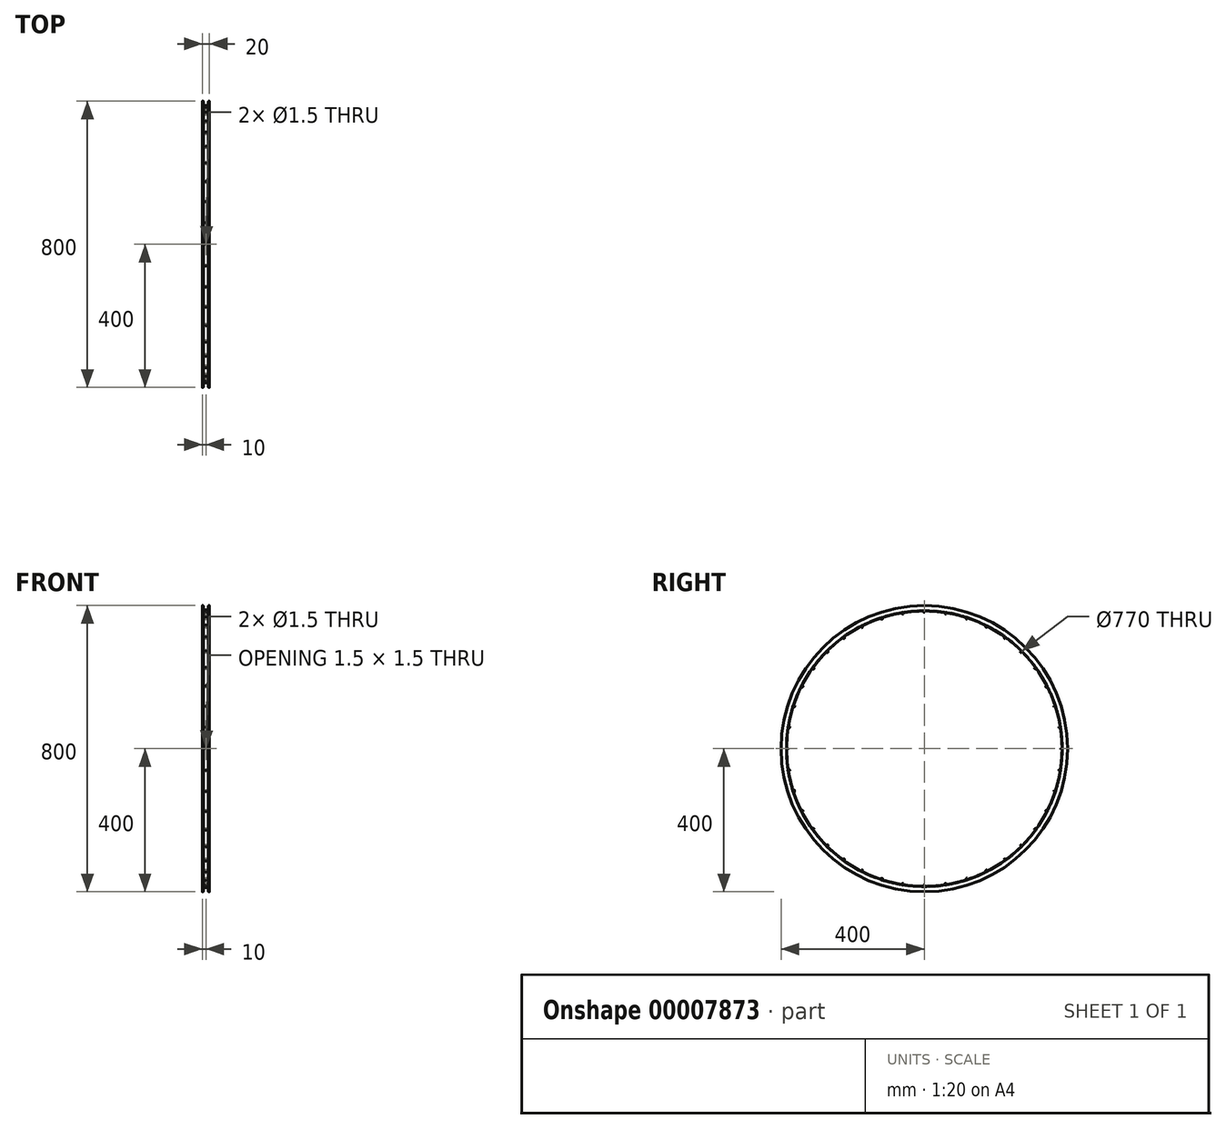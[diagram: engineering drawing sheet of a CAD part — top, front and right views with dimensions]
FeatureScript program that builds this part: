
annotation { "Feature Type Name" : "Feature", "Feature Type Description" : "" }
export const myFeature = defineFeature(function(context is Context, id is Id, definition is map)
    precondition{}
    {
        {
            var Q0;
            Q0=qCreatedBy(makeId("Front.planeOp"),FACE);
            var sketch = newSketch(context, id + "F0", { "sketchPlane" : qUnion([Q0])});
            skLineSegment(sketch, "E0", {"start": v(-99.93, 0) * mm, "end": v(99.93, 0) * mm, "construction": true});
            skLineSegment(sketch, "E1", {"start": v(-10, 385) * mm, "end": v(-10, 400) * mm});
            skLineSegment(sketch, "E2", {"start": v(10, 385) * mm, "end": v(10, 400) * mm});
            skLineSegment(sketch, "E3", {"start": v(0, 0) * mm, "end": v(0, 385) * mm, "construction": true});
            skLineSegment(sketch, "E4", {"start": v(-10, 385) * mm, "end": v(10, 385) * mm});
            skPoint(sketch, "E5", {"position": v(0, 385) * mm});
            skLineSegment(sketch, "E6.0", {"start": v(-7.5, 387.5) * mm, "end": v(-7.5, 400) * mm});
            skLineSegment(sketch, "E6.1", {"start": v(-7.5, 387.5) * mm, "end": v(7.5, 387.5) * mm});
            skLineSegment(sketch, "E6.2", {"start": v(7.5, 387.5) * mm, "end": v(7.5, 400) * mm});
            skLineSegment(sketch, "E7", {"start": v(-10, 400) * mm, "end": v(-7.5, 400) * mm});
            skLineSegment(sketch, "E8", {"start": v(7.5, 400) * mm, "end": v(10, 400) * mm});
            skSolve(sketch);
        }
        {
            var Q0;
            Q0=makeQuery(id+"F0.imprint","IMPRINT",FACE,{"disambiguationData":[TD([[makeQuery(id+"F0.imprint","IMPRINT",EDGE,{"derivedFrom":sQuery(id+"F0.wireOp",EDGE,"E1")}),-1.0]])]});
            var Q1;
            Q1=sQuery(id+"F0.wireOp",EDGE,"E0");
            revolve(context, id + "F1", {"entities" : qUnion([Q0]), "axis" : qUnion([Q1]), "revolveType" : RevolveType.FULL});
        }
        {
            var Q0;
            Q0=makeQuery(id+"F1.opRevolve","SWEPT_EDGE",EDGE,{"disambiguationData":[OSD([sQuery(id+"F0.wireOp",EDGE,"E2"),sQuery(id+"F0.wireOp",EDGE,"E4")])]});
            var Q1;
            Q1=makeQuery(id+"F1.opRevolve","SWEPT_EDGE",EDGE,{"disambiguationData":[OSD([sQuery(id+"F0.wireOp",EDGE,"E6.1"),sQuery(id+"F0.wireOp",EDGE,"E6.2")])]});
            var Q2;
            Q2=makeQuery(id+"F1.opRevolve","SWEPT_EDGE",EDGE,{"disambiguationData":[OSD([sQuery(id+"F0.wireOp",EDGE,"E6.0"),sQuery(id+"F0.wireOp",EDGE,"E6.1")])]});
            var Q3;
            Q3=makeQuery(id+"F1.opRevolve","SWEPT_EDGE",EDGE,{"disambiguationData":[OSD([sQuery(id+"F0.wireOp",EDGE,"E1"),sQuery(id+"F0.wireOp",EDGE,"E4")])]});
            fillet(context, id + "F2", {"entities" : qUnion([Q0, Q1, Q2, Q3]), "radius" : 1.5 * mm, "tangentPropagation" : true, "allowEdgeOverflow" : false});
        }
        {
            var Q0;
            Q0=makeQuery(id+"F1.opRevolve","SWEPT_FACE",FACE,{"disambiguationData":[OSD([sQuery(id+"F0.wireOp",EDGE,"E7")])]});
            var Q1;
            Q1=makeQuery(id+"F1.opRevolve","SWEPT_FACE",FACE,{"disambiguationData":[OSD([sQuery(id+"F0.wireOp",EDGE,"E8")])]});
            fillet(context, id + "F3", {"entities" : qUnion([Q0, Q1]), "radius" : .75 * mm, "tangentPropagation" : true, "allowEdgeOverflow" : false});
        }
        {
            var Q0;
            Q0=qCreatedBy(makeId("Front.planeOp"),FACE);
            var sketch = newSketch(context, id + "F4", { "sketchPlane" : qUnion([Q0])});
            skLineSegment(sketch, "E9", {"start": v(0, 385) * mm, "end": v(2, 385) * mm});
            skLineSegment(sketch, "E10", {"start": v(2, 385) * mm, "end": v(1.65, 381) * mm});
            skLineSegment(sketch, "E11", {"start": v(1.65, 381) * mm, "end": v(0, 381) * mm});
            skLineSegment(sketch, "E12", {"start": v(0, 381) * mm, "end": v(0, 385) * mm});
            skSolve(sketch);
        }
        {
            var Q0;
            Q0=makeQuery(id+"F4.imprint","IMPRINT",FACE,{"disambiguationData":[TD([[makeQuery(id+"F4.imprint","IMPRINT",EDGE,{"derivedFrom":sQuery(id+"F4.wireOp",EDGE,"E9")}),-1.0]])]});
            var Q1;
            Q1=sQuery(id+"F0.wireOp",EDGE,"E3");
            revolve(context, id + "F5", {"operationType" : NewBodyOperationType.ADD, "entities" : qUnion([Q0]), "axis" : qUnion([Q1]), "revolveType" : RevolveType.FULL});
        }
        {
            var Q0;
            Q0=qCreatedBy(makeId("Top.planeOp"),FACE);
            var sketch = newSketch(context, id + "F6", { "sketchPlane" : qUnion([Q0])});
            skCircle(sketch, "E13", {"center": v(0, 0) * mm, "radius": 0.75 * mm});
            skSolve(sketch);
        }
        {
            var Q0;
            Q0=qSketchRegion(id+"F6",true);
            var Q1;
            Q1=makeQuery(id+"F1.opRevolve","SWEPT_FACE",FACE,{"disambiguationData":[OSD([sQuery(id+"F0.wireOp",EDGE,"E6.1")])]});
            extrude(context, id + "F7", {"entities" : qUnion([Q0]), "operationType" : NewBodyOperationType.REMOVE, "endBound" : BoundingType.UP_TO_SURFACE, "endBoundEntityFace" : qUnion([Q1]), "depth" : 25 * mm});
        }
        {
            var Q0;
            Q0=makeQuery(id+"F5.opRevolve","SWEPT_FACE",FACE,{"disambiguationData":[OSD([sQuery(id+"F4.wireOp",EDGE,"E10")])]});
            var Q1;
            Q1=makeQuery(id+"F5.opRevolve","SWEPT_FACE",FACE,{"disambiguationData":[OSD([sQuery(id+"F4.wireOp",EDGE,"E11")])]});
            var Q2;
            Q2=makeQuery(id+"F7.boolean.opBoolean","COPY",FACE,{"derivedFrom":makeQuery(id+"F7.opExtrude","SWEPT_FACE",FACE,{"disambiguationData":[OSD([sQuery(id+"F6.wireOp",EDGE,"E13")])]})});
            var Q3;
            Q3=sQuery(id+"F0.wireOp",EDGE,"E0");
            circularPattern(context, id + "F8", {"faces" : qUnion([Q0, Q1, Q2]), "axis" : qUnion([Q3]), "angle" : 360 * degree, "instanceCount" : round(40), "equalSpace" : true, "patternType" : PatternType.FACE});
        }
    });
